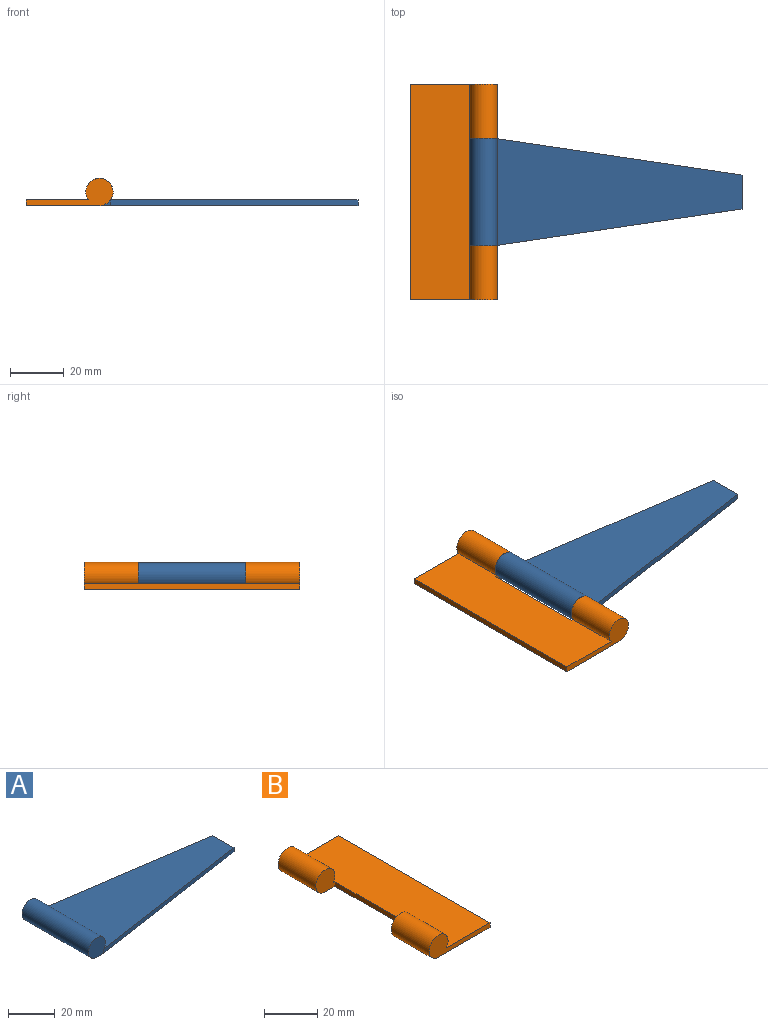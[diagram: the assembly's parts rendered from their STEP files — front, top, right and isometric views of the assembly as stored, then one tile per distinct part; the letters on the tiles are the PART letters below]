
ASSEMBLY  parts=2 mates=1
PART A: 8 faces, bbox 101.6x40.1x10.2 mm
  f0: plane 12.7x2.16mm, normal (1,0,0), area 27.4mm2, adj f3,f5,f6,f7
  f1: plane 10.16x10.16mm, normal (0,-1,0), area 83.8mm2, adj f3,f4,f6
  f2: plane 10.16x10.16mm, normal (0,1,0), area 83.8mm2, adj f3,f4,f7
  f3: plane 96.52x40.13mm, normal (0,0,-1), area 2606.7mm2, adj f0,f1,f2,f4,f6,f7
  f4: cylinder r=5.08mm len=40.13mm, axis (0,1,0), area 1085.6mm2, adj f1,f2,f3,f5
  f5: plane 92.36x40.13mm, normal (0,0,1), area 2439.9mm2, adj f0,f4,f6,f7
  f6: plane 92.36x13.72mm, normal (0.15,-0.99,0), area 201.6mm2, adj f0,f1,f3,f5
  f7: plane 92.36x13.72mm, normal (0.15,0.99,0), area 201.6mm2, adj f0,f2,f3,f5
PART B: 10 faces, bbox 32.5x80.5x10.2 mm
  f0: cylinder r=5.08mm len=20.19mm, axis (0,1,0), area 546.2mm2, adj f2,f3,f5,f7
  f1: cylinder r=5.08mm len=20.19mm, axis (0,1,0), area 546.2mm2, adj f2,f3,f6,f8
  f2: plane 80.52x23.28mm, normal (0,0,1), area 1837mm2, adj f0,f1,f4,f5,f6,f7,f8,f9
  f3: plane 80.52x27.43mm, normal (0,0,-1), area 2004.9mm2, adj f0,f1,f4,f5,f6,f7,f8,f9
  f4: plane 80.52x2.16mm, normal (1,0,0), area 173.8mm2, adj f2,f3,f5,f6
  f5: plane 32.51x10.16mm, normal (0,-1,0), area 134mm2, adj f0,f2,f3,f4
  f6: plane 32.51x10.16mm, normal (0,1,0), area 134mm2, adj f1,f2,f3,f4
  f7: plane 10.16x10.16mm, normal (0,1,0), area 85.7mm2, adj f0,f2,f3,f9
  f8: plane 10.16x10.16mm, normal (0,-1,0), area 85.7mm2, adj f1,f2,f3,f9
  f9: plane 40.13x2.16mm, normal (-1,0,0), area 86.6mm2, adj f2,f3,f7,f8
PLACE A t=(-23.37,60.33,-2.16)mm
PLACE B rot(axis=(0,0,1),180deg) t=(230.63,0,-2.16)mm
MATE revolute B.f0 <-> A.f4  axis (0,-1,0) through (27.43,60.33,2.92)mm
